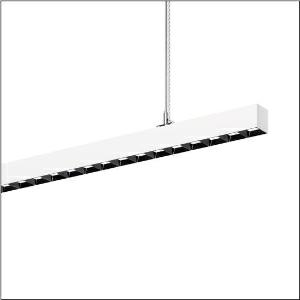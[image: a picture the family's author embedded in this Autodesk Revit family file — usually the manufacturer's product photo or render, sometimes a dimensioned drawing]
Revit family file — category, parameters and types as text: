
# Revit family: silica_r__21_51mx32dc4dwb_0a61
name_source: partatom
category: Lighting Fixtures
units: mm (PartAtom-declared; Revit-internal decimal feet)

## family parameters
Cut with Voids When Loaded = No
Host = Face
Light Source = No
Part Type = Normal
Room Calculation Point = No
Round Connector Dimension = Use Diameter
Shared = No

## types (1)
- --- (1 x LED, 18230 lm, 105.8 W, 4000K)
    Apparent Load = 106 VA
    CIE Flux Codes = 86 99 100 59 100
    Color Rendering = 80
    Color Temperature = 4000K
    Default Elevation = 1800 mm
    Description = Silica® 21, office luminaire, primary light control with darklight reflector, of PMMA, black, CAT 2 (L<= 3000cd/m²), light emission: direct/indirect distribution, primary light characteristic: symmetric, installation type: suspended mounting, LED, rated luminous flux: 18.230lm, luminous efficacy: 172lm/W, light colour: 840, colour temperature: 4000K, with terminal, 3+2-pole, max. 2.5mm², mains connection: 220..240V, AC, 50/60Hz, rated input power: 105.8W, luminaire housing, of aluminium, traffic white (RAL 9016), length: 3.004mm, width: 53mm, height: 53mm, protection rating (complete): IP20, insulation class (complete): insulation class I (protective earthing), certification: CE, permissible operating ambient temperature: 0..+35°C, standard: EN 50419, packaging unit: 1 piece
    Height = 53 mm
    Lamp = 1 x LED
    Lamp Light Flux = 18230 lm
    Lamp Power = 105.8 W
    Lamp count = 1
    Length = 3004 mm
    Luminous efficacy = 172 lm/W
    Manufacturer = Siteco
    ModVariant = No
    Model = 51MX32DC4DWB
    Mounting Place = Ceiling
    Mounting Type = Pendant
    Number of Poles = 1
    OnlyDefault = Yes
    Power Factor = 1
    Product Name = Silica® 21
    Product group = office luminaire | ceiling pendant
    ProductGroupID = 902
    Protection Class = Protection class I
    Protection Degree = IP 20
    RLX_Detail_Level = 1
    RLX_Emergency_Light_Flux = 0 lm
    RLX_Emergency_Type = 0
    RLX_Emergency_Type_DB = No
    RlxData = <blob elided: 64397 chars, md5=ee4ab244>
    Socket = socket
    Standby Power = 0 W
    System Light Flux = 18230 lm
    System Power = 106 W
    Type Comments = factory setting: luminous flux: 100 % | dim-lin: 254 | 366 mA
    Type Image = l_1297801.jpg
    URL = http://relux.com
    VarID = @adj_052931
    Voltage = 0 V
    Weight = 0.00 kg
    Width = 53 mm

## geometry (parser evidence)
native form markers: Blend x4, Sweep x12
no freeform markers — native parametric forms only
